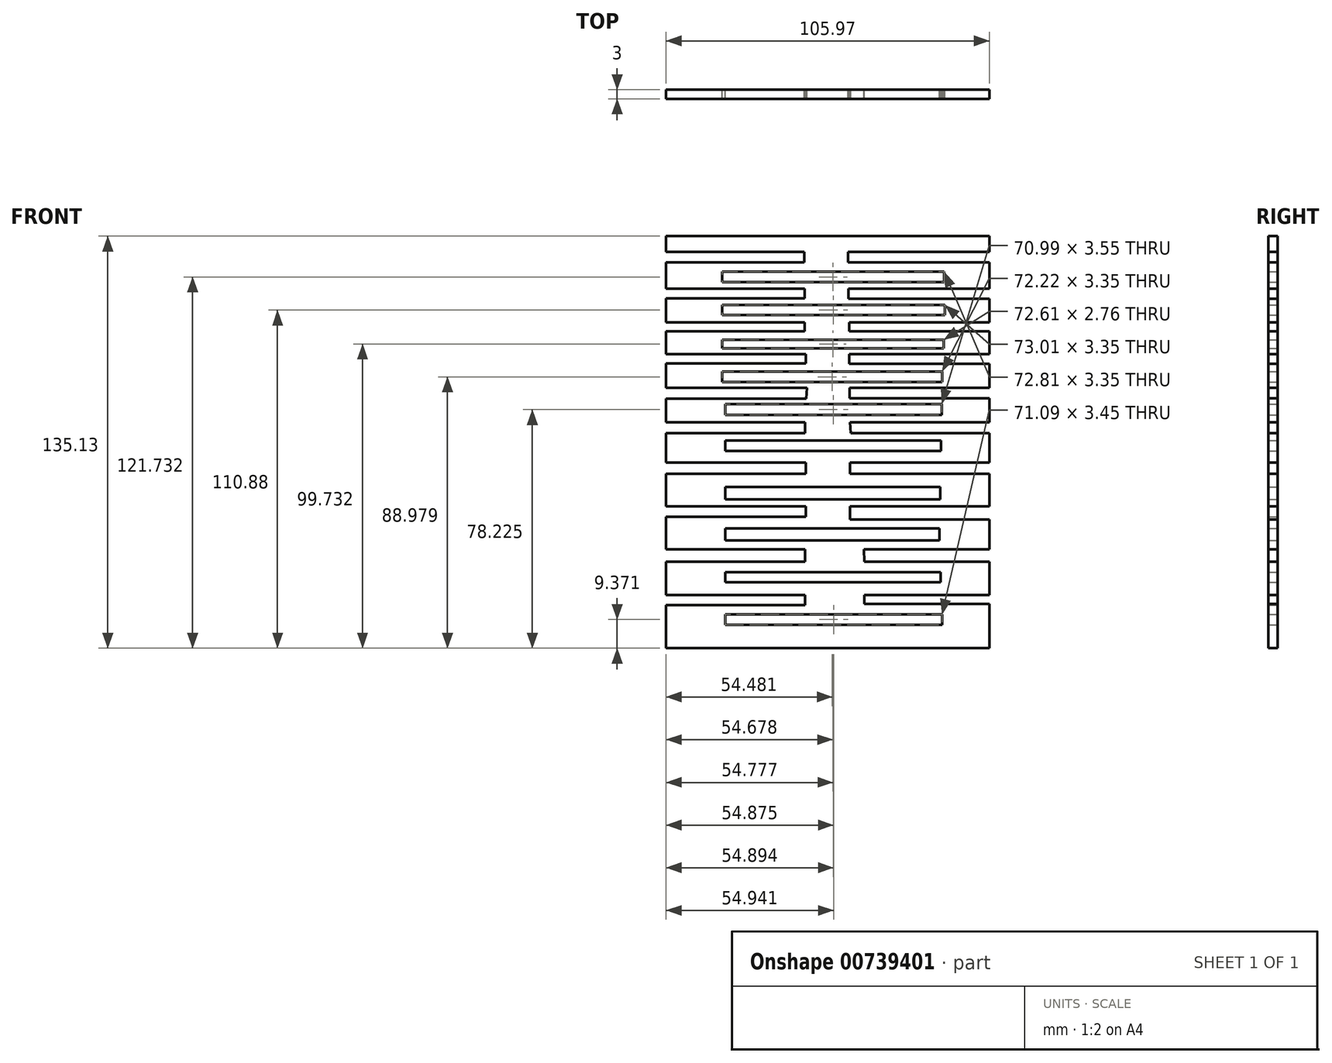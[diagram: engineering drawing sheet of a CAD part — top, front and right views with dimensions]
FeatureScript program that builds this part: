
annotation { "Feature Type Name" : "Feature", "Feature Type Description" : "" }
export const myFeature = defineFeature(function(context is Context, id is Id, definition is map)
    precondition{}
    {
        {
            var Q0;
            Q0=qCreatedBy(makeId("Front.planeOp"),FACE);
            var sketch = newSketch(context, id + "F0", { "sketchPlane" : qUnion([Q0])});
            skLineSegment(sketch, "E0.bottom", {"start": v(-53.8, 64.6) * mm, "end": v(52.18, 64.6) * mm});
            skLineSegment(sketch, "E0.top", {"start": v(-53.8, -70.53) * mm, "end": v(52.18, -70.53) * mm});
            skLineSegment(sketch, "E0.left", {"start": v(-53.8, 64.6) * mm, "end": v(-53.8, 59.43) * mm});
            skLineSegment(sketch, "E0.right", {"start": v(52.18, 64.6) * mm, "end": v(52.18, 59.43) * mm});
            skLineSegment(sketch, "E1.bottom", {"start": v(-34.4, -45.62) * mm, "end": v(36.2, -45.62) * mm});
            skLineSegment(sketch, "E1.top", {"start": v(-34.4, -48.93) * mm, "end": v(36.2, -48.93) * mm});
            skLineSegment(sketch, "E1.left", {"start": v(-34.4, -45.62) * mm, "end": v(-34.4, -48.93) * mm});
            skLineSegment(sketch, "E1.right", {"start": v(36.2, -45.62) * mm, "end": v(36.2, -48.93) * mm});
            skLineSegment(sketch, "E2.bottom", {"start": v(52.18, -38.13) * mm, "end": v(11.08, -38.13) * mm});
            skLineSegment(sketch, "E2.top", {"start": v(52.18, -42.16) * mm, "end": v(11.2, -42.16) * mm});
            skLineSegment(sketch, "E2.right", {"start": v(11.08, -38.13) * mm, "end": v(11.2, -42.16) * mm});
            skLineSegment(sketch, "E3.bottom", {"start": v(-53.8, -38.13) * mm, "end": v(-8.2, -38.13) * mm});
            skLineSegment(sketch, "E3.top", {"start": v(-53.8, -42.16) * mm, "end": v(-8.2, -42.16) * mm});
            skLineSegment(sketch, "E3.right", {"start": v(-8.2, -38.13) * mm, "end": v(-8.2, -42.16) * mm});
            skLineSegment(sketch, "E4.trimOffspring", {"start": v(-53.8, -42.16) * mm, "end": v(-53.8, -53.08) * mm});
            skLineSegment(sketch, "E5.trimOffspring", {"start": v(52.18, -42.16) * mm, "end": v(52.18, -53.08) * mm});
            skLineSegment(sketch, "E6.bottom", {"start": v(-34.4, -31.23) * mm, "end": v(35.83, -31.23) * mm});
            skLineSegment(sketch, "E6.top", {"start": v(-34.4, -35.26) * mm, "end": v(35.83, -35.26) * mm});
            skLineSegment(sketch, "E6.left", {"start": v(-34.4, -31.23) * mm, "end": v(-34.4, -35.26) * mm});
            skLineSegment(sketch, "E6.right", {"start": v(35.83, -31.23) * mm, "end": v(35.83, -35.26) * mm});
            skLineSegment(sketch, "E7.bottom", {"start": v(52.18, -24.03) * mm, "end": v(6.48, -24.03) * mm});
            skLineSegment(sketch, "E7.top", {"start": v(52.18, -28.35) * mm, "end": v(6.48, -28.35) * mm});
            skLineSegment(sketch, "E7.right", {"start": v(6.48, -24.03) * mm, "end": v(6.48, -28.35) * mm});
            skLineSegment(sketch, "E8.bottom", {"start": v(-53.8, -24.03) * mm, "end": v(-7.91, -24.03) * mm});
            skLineSegment(sketch, "E8.top", {"start": v(-53.8, -27.49) * mm, "end": v(-7.91, -27.49) * mm});
            skLineSegment(sketch, "E8.right", {"start": v(-7.91, -24.03) * mm, "end": v(-7.91, -27.49) * mm});
            skLineSegment(sketch, "E9.bottom", {"start": v(-34.4, -17.7) * mm, "end": v(36.12, -17.7) * mm});
            skLineSegment(sketch, "E9.top", {"start": v(-34.4, -21.73) * mm, "end": v(36.12, -21.73) * mm});
            skLineSegment(sketch, "E9.left", {"start": v(-34.4, -17.7) * mm, "end": v(-34.4, -21.73) * mm});
            skLineSegment(sketch, "E9.right", {"start": v(36.12, -17.7) * mm, "end": v(36.12, -21.73) * mm});
            skLineSegment(sketch, "E10.bottom", {"start": v(-7.91, -9.64) * mm, "end": v(-53.8, -9.64) * mm});
            skLineSegment(sketch, "E10.top", {"start": v(-7.91, -13.38) * mm, "end": v(-53.8, -13.38) * mm});
            skLineSegment(sketch, "E10.left", {"start": v(-7.91, -9.64) * mm, "end": v(-7.91, -13.38) * mm});
            skLineSegment(sketch, "E11.bottom", {"start": v(6.48, -9.64) * mm, "end": v(52.18, -9.64) * mm});
            skLineSegment(sketch, "E11.top", {"start": v(6.48, -13.38) * mm, "end": v(52.18, -13.38) * mm});
            skLineSegment(sketch, "E11.left", {"start": v(6.48, -9.64) * mm, "end": v(6.48, -13.38) * mm});
            skLineSegment(sketch, "E12.trimOffspring", {"start": v(-53.8, -13.38) * mm, "end": v(-53.8, -24.03) * mm});
            skLineSegment(sketch, "E13.trimOffspring", {"start": v(52.18, -13.38) * mm, "end": v(52.18, -24.03) * mm});
            skLineSegment(sketch, "E14.bottom", {"start": v(-34.4, -2.45) * mm, "end": v(36.4, -2.45) * mm});
            skLineSegment(sketch, "E14.top", {"start": v(-34.4, -5.9) * mm, "end": v(36.4, -5.9) * mm});
            skLineSegment(sketch, "E14.left", {"start": v(-34.4, -2.45) * mm, "end": v(-34.4, -5.9) * mm});
            skLineSegment(sketch, "E14.right", {"start": v(36.4, -2.45) * mm, "end": v(36.4, -5.9) * mm});
            skLineSegment(sketch, "E15.bottom", {"start": v(-53.8, 3.6) * mm, "end": v(-8.2, 3.6) * mm});
            skLineSegment(sketch, "E15.top", {"start": v(-53.8, 0) * mm, "end": v(-8.2, 0) * mm});
            skLineSegment(sketch, "E15.right", {"start": v(-8.2, 3.6) * mm, "end": v(-8.2, 0) * mm});
            skLineSegment(sketch, "E16.trimOffspring", {"start": v(-53.8, 0) * mm, "end": v(-53.8, -9.64) * mm});
            skLineSegment(sketch, "E17.bottom", {"start": v(52.18, 3.6) * mm, "end": v(6.48, 3.6) * mm});
            skLineSegment(sketch, "E17.top", {"start": v(52.18, 0) * mm, "end": v(6.76, 0) * mm});
            skLineSegment(sketch, "E17.right", {"start": v(6.48, 3.6) * mm, "end": v(6.76, 0) * mm});
            skLineSegment(sketch, "E18.trimOffspring", {"start": v(52.18, 0) * mm, "end": v(52.18, -9.64) * mm});
            skLineSegment(sketch, "E19.trimOffspring", {"start": v(52.18, -28.35) * mm, "end": v(52.18, -38.13) * mm});
            skLineSegment(sketch, "E20.trimOffspring", {"start": v(-53.8, -27.49) * mm, "end": v(-53.8, -38.13) * mm});
            skLineSegment(sketch, "E21.bottom", {"start": v(-34.4, 9.47) * mm, "end": v(36.6, 9.47) * mm});
            skLineSegment(sketch, "E21.top", {"start": v(-34.4, 5.92) * mm, "end": v(36.6, 5.92) * mm});
            skLineSegment(sketch, "E21.left", {"start": v(-34.4, 9.47) * mm, "end": v(-34.4, 5.92) * mm});
            skLineSegment(sketch, "E21.right", {"start": v(36.6, 9.47) * mm, "end": v(36.6, 5.92) * mm});
            skLineSegment(sketch, "E22.bottom", {"start": v(-53.8, 14.8) * mm, "end": v(-7.6, 14.8) * mm});
            skLineSegment(sketch, "E22.top", {"start": v(-53.8, 11.25) * mm, "end": v(-7.8, 11.25) * mm});
            skLineSegment(sketch, "E22.right", {"start": v(-7.6, 14.8) * mm, "end": v(-7.8, 11.25) * mm});
            skLineSegment(sketch, "E23.trimOffspring", {"start": v(-53.8, 11.25) * mm, "end": v(-53.8, 3.6) * mm});
            skLineSegment(sketch, "E24.bottom", {"start": v(52.18, 14.8) * mm, "end": v(6.41, 14.8) * mm});
            skLineSegment(sketch, "E24.top", {"start": v(52.18, 11.44) * mm, "end": v(6.41, 11.44) * mm});
            skLineSegment(sketch, "E24.right", {"start": v(6.41, 14.8) * mm, "end": v(6.41, 11.44) * mm});
            skLineSegment(sketch, "E25.trimOffspring", {"start": v(52.18, 11.44) * mm, "end": v(52.18, 3.6) * mm});
            skLineSegment(sketch, "E26.bottom", {"start": v(-35.42, 20.13) * mm, "end": v(36.8, 20.13) * mm});
            skLineSegment(sketch, "E26.top", {"start": v(-35.42, 16.77) * mm, "end": v(36.8, 16.77) * mm});
            skLineSegment(sketch, "E26.left", {"start": v(-35.42, 20.13) * mm, "end": v(-35.42, 16.77) * mm});
            skLineSegment(sketch, "E26.right", {"start": v(36.8, 20.13) * mm, "end": v(36.8, 16.77) * mm});
            skLineSegment(sketch, "E27.bottom", {"start": v(-53.8, 25.85) * mm, "end": v(-8, 25.85) * mm});
            skLineSegment(sketch, "E27.top", {"start": v(-53.8, 22.89) * mm, "end": v(-8, 22.89) * mm});
            skLineSegment(sketch, "E27.right", {"start": v(-8, 25.85) * mm, "end": v(-8, 22.89) * mm});
            skLineSegment(sketch, "E28.trimOffspring", {"start": v(-53.8, 22.89) * mm, "end": v(-53.8, 14.8) * mm});
            skLineSegment(sketch, "E29.bottom", {"start": v(52.18, 25.85) * mm, "end": v(6.22, 25.85) * mm});
            skLineSegment(sketch, "E29.top", {"start": v(52.18, 22.7) * mm, "end": v(6.22, 22.7) * mm});
            skLineSegment(sketch, "E29.right", {"start": v(6.22, 25.85) * mm, "end": v(6.22, 22.7) * mm});
            skLineSegment(sketch, "E30.trimOffspring", {"start": v(52.18, 22.7) * mm, "end": v(52.18, 14.8) * mm});
            skLineSegment(sketch, "E31.bottom", {"start": v(-35.42, 30.58) * mm, "end": v(37.2, 30.58) * mm});
            skLineSegment(sketch, "E31.top", {"start": v(-35.42, 27.82) * mm, "end": v(37.2, 27.82) * mm});
            skLineSegment(sketch, "E31.left", {"start": v(-35.42, 30.58) * mm, "end": v(-35.42, 27.82) * mm});
            skLineSegment(sketch, "E31.right", {"start": v(37.2, 30.58) * mm, "end": v(37.2, 27.82) * mm});
            skLineSegment(sketch, "E32.bottom", {"start": v(-53.8, 36.3) * mm, "end": v(-8.39, 36.3) * mm});
            skLineSegment(sketch, "E32.top", {"start": v(-53.8, 33.35) * mm, "end": v(-8.39, 33.35) * mm});
            skLineSegment(sketch, "E32.right", {"start": v(-8.39, 36.3) * mm, "end": v(-8.39, 33.35) * mm});
            skLineSegment(sketch, "E33.trimOffspring", {"start": v(-53.8, 33.35) * mm, "end": v(-53.8, 25.85) * mm});
            skLineSegment(sketch, "E34.bottom", {"start": v(52.18, 36.3) * mm, "end": v(6.22, 36.3) * mm});
            skLineSegment(sketch, "E34.top", {"start": v(52.18, 33.35) * mm, "end": v(6.22, 33.35) * mm});
            skLineSegment(sketch, "E34.right", {"start": v(6.22, 36.3) * mm, "end": v(6.22, 33.35) * mm});
            skLineSegment(sketch, "E35.trimOffspring", {"start": v(52.18, 33.35) * mm, "end": v(52.18, 25.85) * mm});
            skLineSegment(sketch, "E36.bottom", {"start": v(-35.42, 42.03) * mm, "end": v(37.59, 42.03) * mm});
            skLineSegment(sketch, "E36.top", {"start": v(-35.42, 38.67) * mm, "end": v(37.59, 38.67) * mm});
            skLineSegment(sketch, "E36.left", {"start": v(-35.42, 42.03) * mm, "end": v(-35.42, 38.67) * mm});
            skLineSegment(sketch, "E36.right", {"start": v(37.59, 42.03) * mm, "end": v(37.59, 38.67) * mm});
            skLineSegment(sketch, "E37.bottom", {"start": v(-53.8, 47.35) * mm, "end": v(-8.39, 47.35) * mm});
            skLineSegment(sketch, "E37.top", {"start": v(-53.8, 44.2) * mm, "end": v(-8.39, 44.2) * mm});
            skLineSegment(sketch, "E37.right", {"start": v(-8.39, 47.35) * mm, "end": v(-8.39, 44.2) * mm});
            skLineSegment(sketch, "E38.trimOffspring", {"start": v(-53.8, 44.2) * mm, "end": v(-53.8, 36.3) * mm});
            skLineSegment(sketch, "E39.bottom", {"start": v(52.18, 47.35) * mm, "end": v(6.02, 47.35) * mm});
            skLineSegment(sketch, "E39.top", {"start": v(52.18, 44) * mm, "end": v(6.02, 44) * mm});
            skLineSegment(sketch, "E39.right", {"start": v(6.02, 47.35) * mm, "end": v(6.02, 44) * mm});
            skLineSegment(sketch, "E40.trimOffspring", {"start": v(52.18, 44) * mm, "end": v(52.18, 36.3) * mm});
            skLineSegment(sketch, "E41.bottom", {"start": v(-35.42, 52.88) * mm, "end": v(37.4, 52.88) * mm});
            skLineSegment(sketch, "E41.top", {"start": v(-35.42, 49.53) * mm, "end": v(37.4, 49.53) * mm});
            skLineSegment(sketch, "E41.left", {"start": v(-35.42, 52.88) * mm, "end": v(-35.42, 49.53) * mm});
            skLineSegment(sketch, "E41.right", {"start": v(37.4, 52.88) * mm, "end": v(37.4, 49.53) * mm});
            skLineSegment(sketch, "E42.bottom", {"start": v(-8.2, -53.08) * mm, "end": v(-53.8, -53.08) * mm});
            skLineSegment(sketch, "E42.top", {"start": v(-8.2, -56.35) * mm, "end": v(-53.8, -56.35) * mm});
            skLineSegment(sketch, "E42.left", {"start": v(-8.2, -53.08) * mm, "end": v(-8.2, -56.35) * mm});
            skLineSegment(sketch, "E43.bottom", {"start": v(52.18, -53.08) * mm, "end": v(11.2, -53.08) * mm});
            skLineSegment(sketch, "E43.top", {"start": v(52.18, -56.04) * mm, "end": v(11.2, -56.04) * mm});
            skLineSegment(sketch, "E43.right", {"start": v(11.2, -53.08) * mm, "end": v(11.2, -56.04) * mm});
            skLineSegment(sketch, "E44.trimOffspring", {"start": v(-53.8, -56.35) * mm, "end": v(-53.8, -70.53) * mm});
            skLineSegment(sketch, "E45.trimOffspring", {"start": v(52.18, -56.04) * mm, "end": v(52.18, -70.53) * mm});
            skLineSegment(sketch, "E46.bottom", {"start": v(-34.4, -59.43) * mm, "end": v(36.7, -59.43) * mm});
            skLineSegment(sketch, "E46.top", {"start": v(-34.4, -62.89) * mm, "end": v(36.7, -62.89) * mm});
            skLineSegment(sketch, "E46.left", {"start": v(-34.4, -59.43) * mm, "end": v(-34.4, -62.89) * mm});
            skLineSegment(sketch, "E46.right", {"start": v(36.7, -59.43) * mm, "end": v(36.7, -62.89) * mm});
            skPoint(sketch, "E47.oppositeSnap0", {"position": v(-53.8, 55.98) * mm});
            skLineSegment(sketch, "E47.bottom", {"start": v(-53.8, 59.43) * mm, "end": v(-8.5, 59.43) * mm});
            skLineSegment(sketch, "E47.top", {"start": v(-53.8, 55.98) * mm, "end": v(-8.5, 55.98) * mm});
            skLineSegment(sketch, "E47.right", {"start": v(-8.5, 59.43) * mm, "end": v(-8.5, 55.98) * mm});
            skLineSegment(sketch, "E48.bottom", {"start": v(52.18, 59.43) * mm, "end": v(5.9, 59.43) * mm});
            skLineSegment(sketch, "E48.top", {"start": v(52.18, 55.98) * mm, "end": v(5.9, 55.98) * mm});
            skLineSegment(sketch, "E48.right", {"start": v(5.9, 59.43) * mm, "end": v(5.9, 55.98) * mm});
            skLineSegment(sketch, "E49.trimOffspring", {"start": v(52.18, 55.98) * mm, "end": v(52.18, 47.35) * mm});
            skLineSegment(sketch, "E50.trimOffspring", {"start": v(-53.8, 55.98) * mm, "end": v(-53.8, 47.35) * mm});
            skSolve(sketch);
        }
        {
            var Q0;
            Q0=makeQuery(id+"F0.imprint","IMPRINT",FACE,{"disambiguationData":[TD([[makeQuery(id+"F0.imprint","IMPRINT",EDGE,{"derivedFrom":sQuery(id+"F0.wireOp",EDGE,"E0.bottom")}),-1.0]])]});
            extrude(context, id + "F1", {"entities" : qUnion([Q0]), "depth" : 3 * mm, "offsetDistance" : 25.4 * mm});
        }
    });
